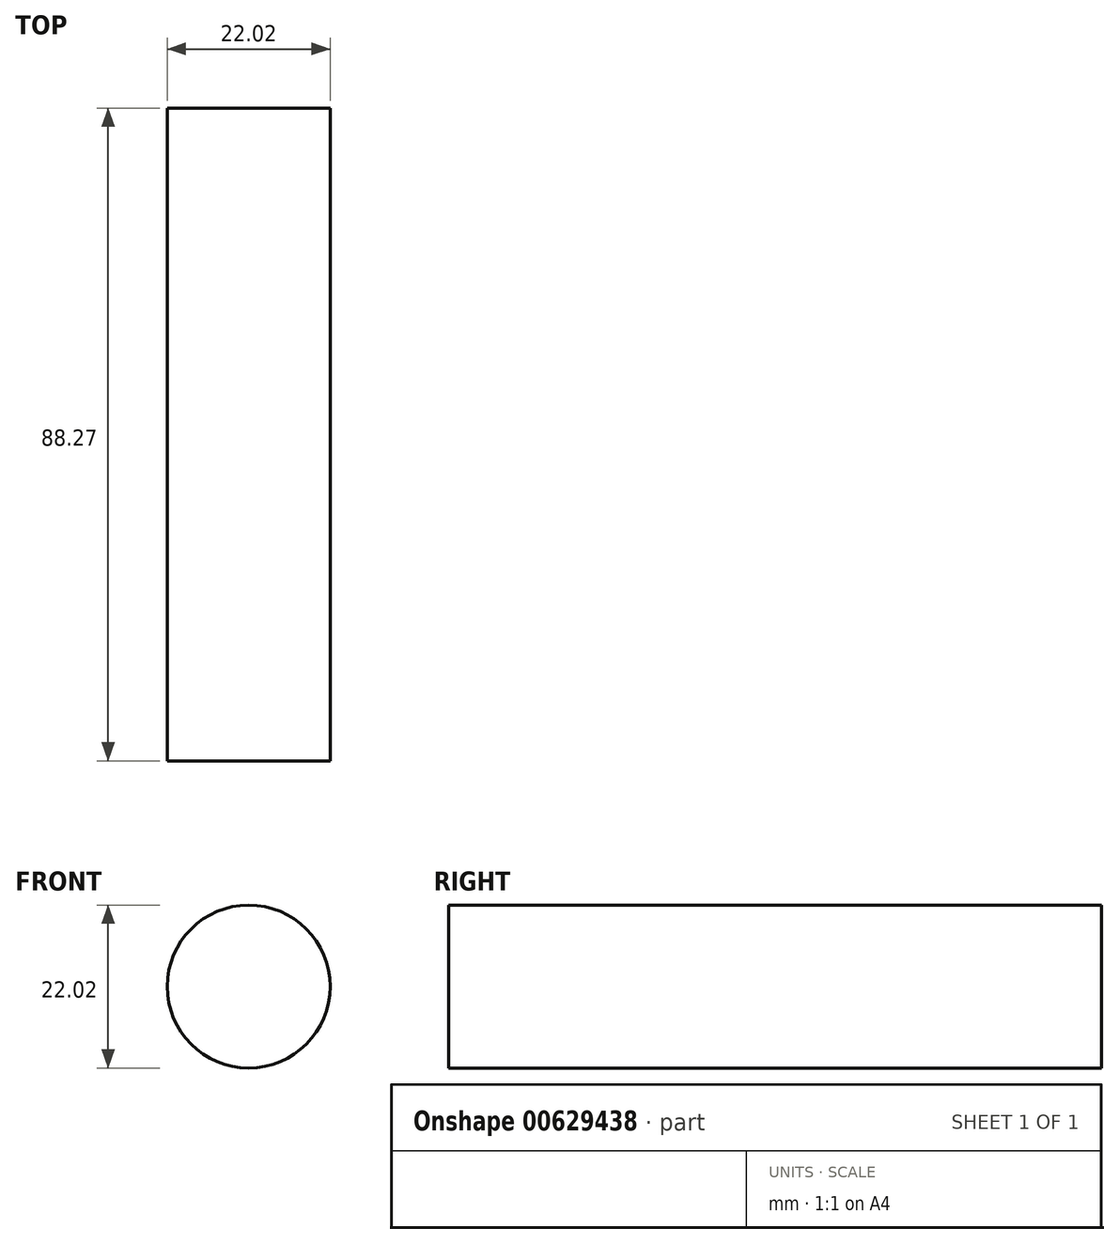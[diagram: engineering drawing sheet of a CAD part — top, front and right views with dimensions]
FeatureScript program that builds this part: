
annotation { "Feature Type Name" : "Feature", "Feature Type Description" : "" }
export const myFeature = defineFeature(function(context is Context, id is Id, definition is map)
    precondition{}
    {
        {
            var Q0;
            Q0=qCreatedBy(makeId("Front.planeOp"),FACE);
            var sketch = newSketch(context, id + "F0", { "sketchPlane" : qUnion([Q0])});
            skCircle(sketch, "E0", {"center": v(0, 0) * mm, "radius": 11.01 * mm});
            skSolve(sketch);
        }
        {
            var Q0;
            Q0 = qSketchRegion(id + "F0", true);
            extrude(context, id + "F1", {"entities" : qUnion([Q0]), "depth" : 88.27 * mm, "offsetDistance" : 25.4 * mm});
        }
    });
